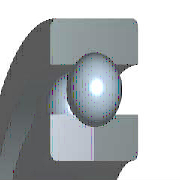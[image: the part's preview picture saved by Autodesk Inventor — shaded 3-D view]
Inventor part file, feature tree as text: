
AUTODESK INVENTOR PART (.ipt)
format: ipt  version: 2015 (Build 190159000, 159)  size: 310,272 bytes
history: native  units: mm (DEFAULTED — no unit token found)
features: sketch x1, other x1, pattern_circular x1
ambient origin geometry x8: Origin, YZ Plane, XZ Plane, XY Plane, X Axis, Y Axis, Z Axis, Center Point
bodies: Body (feature_tree)
feature tree (3):
  sketch  "Sketch"  dims[d9=90.0deg d0=0.3mm d12=90.0deg d1=80.0mm d2=360.0deg d3=4.16mm d4=0.0mm d5=0.0mm d6=0.0mm d7=12.0mm d8=28.0mm d10=8.0mm d11=20.0mm d13=17.216mm d15=22.784mm d16=0.0mm d17=0.0mm]
  other  "Ball"
  pattern_circular  "Balls"  [2 undecoded]
note: 2 required parameter values undecoded (feature->parameter linkage not recoverable at this tier; creation-order binding heuristic only, values carry confidence <= 0.55)
